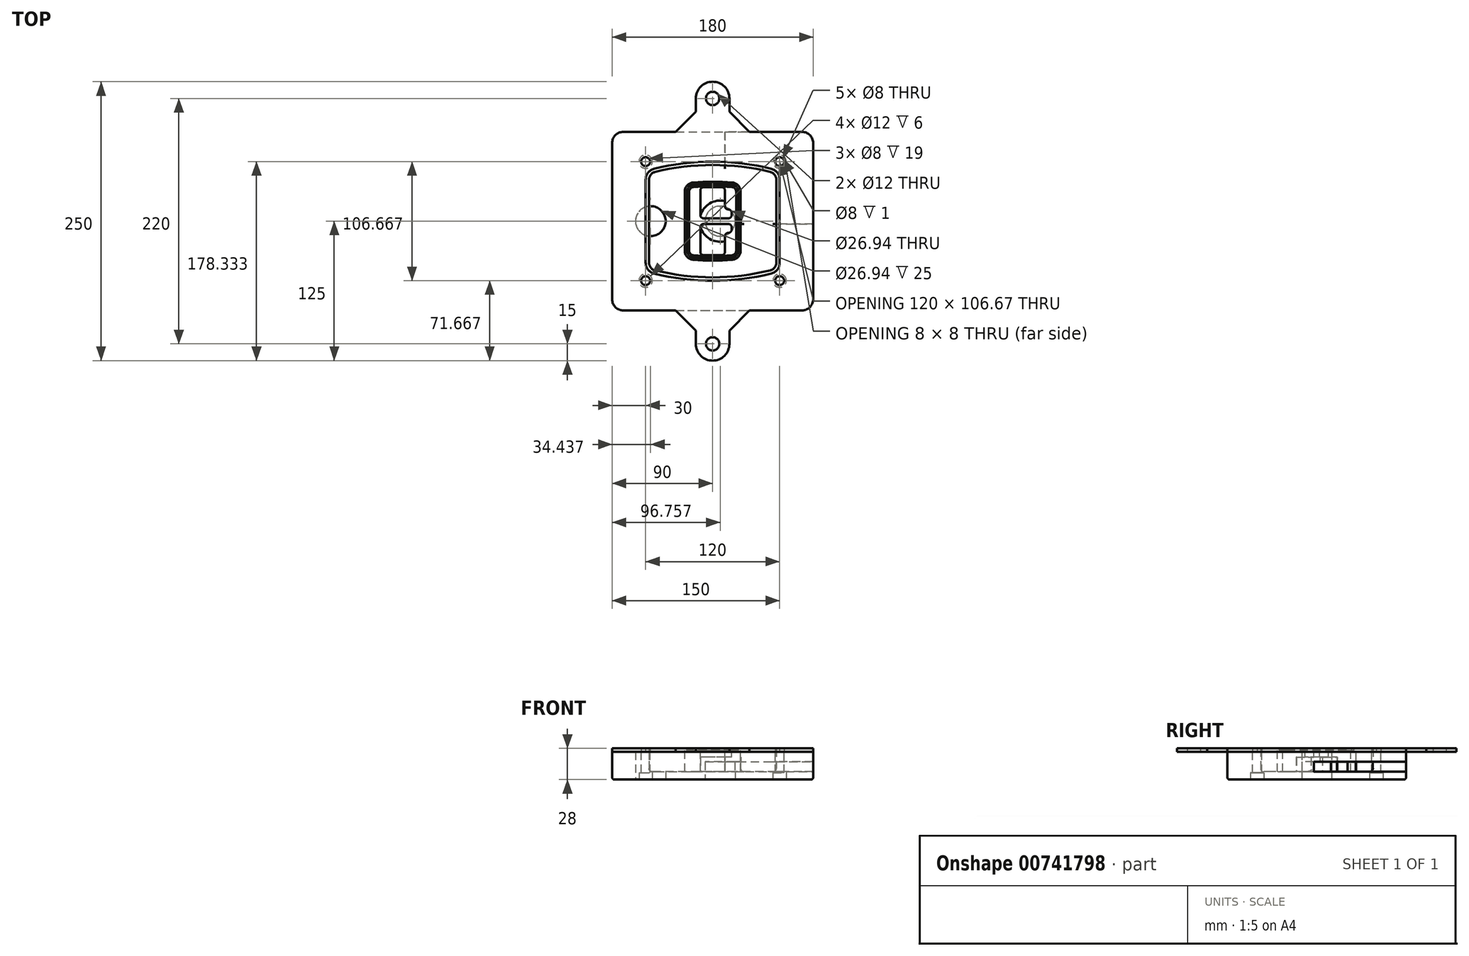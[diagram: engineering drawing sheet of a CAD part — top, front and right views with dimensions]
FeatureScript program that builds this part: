
annotation { "Feature Type Name" : "Feature", "Feature Type Description" : "" }
export const myFeature = defineFeature(function(context is Context, id is Id, definition is map)
    precondition{}
    {
        {
            var Q0;
            Q0=qCreatedBy(makeId("Top.planeOp"),FACE);
            var sketch = newSketch(context, id + "F0", { "sketchPlane" : qUnion([Q0])});
            skPoint(sketch, "E0.rect.middle", {"position": v(0, 0) * mm});
            skLineSegment(sketch, "E1.bottom", {"start": v(-80, -80) * mm, "end": v(80, -80) * mm});
            skLineSegment(sketch, "E1.top", {"start": v(-80, 80) * mm, "end": v(80, 80) * mm});
            skLineSegment(sketch, "E1.left", {"start": v(-90, -70) * mm, "end": v(-90, 70) * mm});
            skLineSegment(sketch, "E1.right", {"start": v(90, -70) * mm, "end": v(90, 70) * mm});
            skLineSegment(sketch, "E2", {"start": v(-90, 80) * mm, "end": v(90, -80) * mm, "construction": true});
            skLineSegment(sketch, "E3", {"start": v(90, 80) * mm, "end": v(-90, -80) * mm, "construction": true});
            skCircle(sketch, "E4", {"center": v(-60, 53.33) * mm, "radius": 4 * mm});
            skCircle(sketch, "E5", {"center": v(60, 53.33) * mm, "radius": 4 * mm});
            skCircle(sketch, "E6", {"center": v(60, -53.33) * mm, "radius": 4 * mm});
            skCircle(sketch, "E7", {"center": v(-60, -53.33) * mm, "radius": 4 * mm});
            skLineSegment(sketch, "E8", {"start": v(-60, 53.33) * mm, "end": v(60, 53.33) * mm, "construction": true});
            skLineSegment(sketch, "E9", {"start": v(60, 53.33) * mm, "end": v(60, -53.33) * mm, "construction": true});
            skLineSegment(sketch, "E10", {"start": v(60, -53.33) * mm, "end": v(-60, -53.33) * mm, "construction": true});
            skLineSegment(sketch, "E11", {"start": v(-60, -53.33) * mm, "end": v(-60, 53.33) * mm, "construction": true});
            skLineSegment(sketch, "E12", {"start": v(-60, 37.3) * mm, "end": v(-60, -37.3) * mm});
            skLineSegment(sketch, "E13", {"start": v(60, 37.3) * mm, "end": v(60, -37.3) * mm});
            skArc(sketch, "E14", {"start": v(52.38, 47.01) * mm, "mid": v(0, 53.33) * mm, "end": v(-52.38, 47.01) * mm});
            skArc(sketch, "E15", {"start": v(-52.38, -47.01) * mm, "mid": v(0, -53.33) * mm, "end": v(52.38, -47.01) * mm});
            skLineSegment(sketch, "E16", {"start": v(-60, 0) * mm, "end": v(60, 0) * mm, "construction": true});
            skPoint(sketch, "E17.visualSharp", {"position": v(-60, -45) * mm});
            skArc(sketch, "E17.filletArc", {"start": v(-60, -37.3) * mm, "mid": v(-57.87, -43.47) * mm, "end": v(-52.38, -47.01) * mm});
            skPoint(sketch, "E18.visualSharp", {"position": v(-60, 45) * mm});
            skArc(sketch, "E18.filletArc", {"start": v(-52.38, 47.01) * mm, "mid": v(-57.87, 43.47) * mm, "end": v(-60, 37.3) * mm});
            skPoint(sketch, "E19.visualSharp", {"position": v(60, 45) * mm});
            skArc(sketch, "E19.filletArc", {"start": v(60, 37.3) * mm, "mid": v(57.87, 43.47) * mm, "end": v(52.38, 47.01) * mm});
            skPoint(sketch, "E20.visualSharp", {"position": v(60, -45) * mm});
            skArc(sketch, "E20.filletArc", {"start": v(52.38, -47.01) * mm, "mid": v(57.87, -43.47) * mm, "end": v(60, -37.3) * mm});
            skPoint(sketch, "E21.visualSharp", {"position": v(-90, 80) * mm});
            skArc(sketch, "E21.filletArc", {"start": v(-80, 80) * mm, "mid": v(-87.07, 77.07) * mm, "end": v(-90, 70) * mm});
            skPoint(sketch, "E22.visualSharp", {"position": v(90, 80) * mm});
            skArc(sketch, "E22.filletArc", {"start": v(90, 70) * mm, "mid": v(87.07, 77.07) * mm, "end": v(80, 80) * mm});
            skPoint(sketch, "E23.visualSharp", {"position": v(90, -80) * mm});
            skArc(sketch, "E23.filletArc", {"start": v(80, -80) * mm, "mid": v(87.07, -77.07) * mm, "end": v(90, -70) * mm});
            skPoint(sketch, "E24.visualSharp", {"position": v(-90, -80) * mm});
            skArc(sketch, "E24.filletArc", {"start": v(-90, -70) * mm, "mid": v(-87.07, -77.07) * mm, "end": v(-80, -80) * mm});
            skArc(sketch, "E25.0", {"start": v(57, 37.3) * mm, "mid": v(55.5, 41.62) * mm, "end": v(51.67, 44.1) * mm});
            skLineSegment(sketch, "E25.1", {"start": v(57, 37.3) * mm, "end": v(57, -37.3) * mm});
            skArc(sketch, "E25.2", {"start": v(51.67, -44.1) * mm, "mid": v(55.5, -41.62) * mm, "end": v(57, -37.3) * mm});
            skArc(sketch, "E25.3", {"start": v(-51.67, -44.1) * mm, "mid": v(0, -50.33) * mm, "end": v(51.67, -44.1) * mm});
            skArc(sketch, "E25.4", {"start": v(-57, -37.3) * mm, "mid": v(-55.5, -41.62) * mm, "end": v(-51.67, -44.1) * mm});
            skArc(sketch, "E25.5", {"start": v(51.67, 44.1) * mm, "mid": v(0, 50.33) * mm, "end": v(-51.67, 44.1) * mm});
            skLineSegment(sketch, "E25.6", {"start": v(-57, 37.3) * mm, "end": v(-57, -37.3) * mm});
            skArc(sketch, "E25.7", {"start": v(-51.67, 44.1) * mm, "mid": v(-55.5, 41.62) * mm, "end": v(-57, 37.3) * mm});
            skArc(sketch, "E26.0", {"start": v(-53.33, 50.9) * mm, "mid": v(-61.01, 45.94) * mm, "end": v(-64, 37.3) * mm});
            skArc(sketch, "E26.1", {"start": v(53.33, 50.9) * mm, "mid": v(0, 57.33) * mm, "end": v(-53.33, 50.9) * mm});
            skArc(sketch, "E26.2", {"start": v(64, 37.3) * mm, "mid": v(61.01, 45.94) * mm, "end": v(53.33, 50.9) * mm});
            skLineSegment(sketch, "E26.3", {"start": v(64, 37.3) * mm, "end": v(64, -37.3) * mm});
            skArc(sketch, "E26.4", {"start": v(53.33, -50.9) * mm, "mid": v(61.01, -45.94) * mm, "end": v(64, -37.3) * mm});
            skLineSegment(sketch, "E26.5", {"start": v(-64, 37.3) * mm, "end": v(-64, -37.3) * mm});
            skArc(sketch, "E26.6", {"start": v(-53.33, -50.9) * mm, "mid": v(0, -57.33) * mm, "end": v(53.33, -50.9) * mm});
            skArc(sketch, "E26.7", {"start": v(-64, -37.3) * mm, "mid": v(-61.01, -45.94) * mm, "end": v(-53.33, -50.9) * mm});
            skSolve(sketch);
        }
        {
            var Q0;
            Q0=makeQuery(id+"F0.imprint","IMPRINT",FACE,{"disambiguationData":[TD([[makeQuery(id+"F0.imprint","IMPRINT",EDGE,{"derivedFrom":sQuery(id+"F0.wireOp",EDGE,"E1.bottom")}),1.0]])]});
            var Q1;
            Q1=makeQuery(id+"F0.imprint","IMPRINT",FACE,{"disambiguationData":[TD([[makeQuery(id+"F0.imprint","IMPRINT",EDGE,{"derivedFrom":sQuery(id+"F0.wireOp",EDGE,"E12")}),1.0]])]});
            var Q2;
            Q2=makeQuery(id+"F0.imprint","IMPRINT",FACE,{"disambiguationData":[TD([[makeQuery(id+"F0.imprint","IMPRINT",EDGE,{"derivedFrom":sQuery(id+"F0.wireOp",EDGE,"E25.0")}),1.0]])]});
            var Q3;
            Q3=makeQuery(id+"F0.imprint","IMPRINT",FACE,{"disambiguationData":[TD([[makeQuery(id+"F0.imprint","IMPRINT",EDGE,{"derivedFrom":sQuery(id+"F0.wireOp",EDGE,"E12")}),-1.0]])]});
            extrude(context, id + "F1", {"entities" : qUnion([Q0, Q1, Q2, Q3]), "oppositeDirection" : true, "depth" : 25 * mm, "offsetDistance" : 25 * mm});
        }
        {
            var Q0;
            Q0=makeQuery(id+"F0.imprint","IMPRINT",FACE,{"disambiguationData":[TD([[makeQuery(id+"F0.imprint","IMPRINT",EDGE,{"derivedFrom":sQuery(id+"F0.wireOp",EDGE,"E12")}),1.0]])]});
            extrude(context, id + "F2", {"entities" : qUnion([Q0]), "operationType" : NewBodyOperationType.ADD, "depth" : 3 * mm});
        }
        {
            var Q0;
            Q0=makeQuery(id+"F0.imprint","IMPRINT",FACE,{"disambiguationData":[TD([[makeQuery(id+"F0.imprint","IMPRINT",EDGE,{"derivedFrom":sQuery(id+"F0.wireOp",EDGE,"E25.0")}),1.0]])]});
            extrude(context, id + "F3", {"entities" : qUnion([Q0]), "operationType" : NewBodyOperationType.REMOVE, "oppositeDirection" : true, "depth" : 18 * mm});
        }
        {
            var Q0;
            Q0=makeQuery(id+"F2.opExtrude","CAP_FACE",FACE,{"disambiguationData":[OSD([sQuery(id+"F0.wireOp",EDGE,"E12"),sQuery(id+"F0.wireOp",EDGE,"E13"),sQuery(id+"F0.wireOp",EDGE,"E14"),sQuery(id+"F0.wireOp",EDGE,"E15"),sQuery(id+"F0.wireOp",EDGE,"E17.filletArc"),sQuery(id+"F0.wireOp",EDGE,"E18.filletArc"),sQuery(id+"F0.wireOp",EDGE,"E19.filletArc"),sQuery(id+"F0.wireOp",EDGE,"E20.filletArc"),sQuery(id+"F0.wireOp",EDGE,"E25.0"),sQuery(id+"F0.wireOp",EDGE,"E25.1"),sQuery(id+"F0.wireOp",EDGE,"E25.2"),sQuery(id+"F0.wireOp",EDGE,"E25.3"),sQuery(id+"F0.wireOp",EDGE,"E25.4"),sQuery(id+"F0.wireOp",EDGE,"E25.5"),sQuery(id+"F0.wireOp",EDGE,"E25.6"),sQuery(id+"F0.wireOp",EDGE,"E25.7")])],"isStart":false});
            var sketch = newSketch(context, id + "F4", { "sketchPlane" : qUnion([Q0])});
            skArc(sketch, "E27.0", {"start": v(-17.7, -34.56) * mm, "mid": v(0, -35.33) * mm, "end": v(17.7, -34.56) * mm});
            skArc(sketch, "E28.0", {"start": v(17.7, 34.56) * mm, "mid": v(0, 35.33) * mm, "end": v(-17.7, 34.56) * mm});
            skLineSegment(sketch, "E29", {"start": v(-25, 26.59) * mm, "end": v(-25, -26.59) * mm});
            skLineSegment(sketch, "E30", {"start": v(25, 26.59) * mm, "end": v(25, -26.59) * mm});
            skLineSegment(sketch, "E31", {"start": v(-25, 33.78) * mm, "end": v(25, 33.78) * mm, "construction": true});
            skLineSegment(sketch, "E32", {"start": v(-25, -33.78) * mm, "end": v(25, -33.78) * mm, "construction": true});
            skPoint(sketch, "E33.visualSharp", {"position": v(-25, 33.78) * mm});
            skArc(sketch, "E33.filletArc", {"start": v(-17.7, 34.56) * mm, "mid": v(-22.9, 32) * mm, "end": v(-25, 26.59) * mm});
            skPoint(sketch, "E34.visualSharp", {"position": v(25, 33.78) * mm});
            skArc(sketch, "E34.filletArc", {"start": v(25, 26.59) * mm, "mid": v(22.9, 32) * mm, "end": v(17.7, 34.56) * mm});
            skPoint(sketch, "E35.visualSharp", {"position": v(25, -33.78) * mm});
            skArc(sketch, "E35.filletArc", {"start": v(17.7, -34.56) * mm, "mid": v(22.9, -32) * mm, "end": v(25, -26.59) * mm});
            skPoint(sketch, "E36.visualSharp", {"position": v(-25, -33.78) * mm});
            skArc(sketch, "E36.filletArc", {"start": v(-25, -26.59) * mm, "mid": v(-22.9, -32) * mm, "end": v(-17.7, -34.56) * mm});
            skArc(sketch, "E37.0", {"start": v(51.67, 44.1) * mm, "mid": v(0, 50.33) * mm, "end": v(-51.67, 44.1) * mm});
            skArc(sketch, "E37.1", {"start": v(-51.67, 44.1) * mm, "mid": v(-55.5, 41.62) * mm, "end": v(-57, 37.3) * mm});
            skLineSegment(sketch, "E37.2", {"start": v(-57, 37.3) * mm, "end": v(-57, -37.3) * mm});
            skArc(sketch, "E37.3", {"start": v(-57, -37.3) * mm, "mid": v(-55.5, -41.62) * mm, "end": v(-51.67, -44.1) * mm});
            skArc(sketch, "E37.4", {"start": v(-51.67, -44.1) * mm, "mid": v(0, -50.33) * mm, "end": v(51.67, -44.1) * mm});
            skArc(sketch, "E37.5", {"start": v(51.67, -44.1) * mm, "mid": v(55.5, -41.62) * mm, "end": v(57, -37.3) * mm});
            skLineSegment(sketch, "E37.6", {"start": v(57, 37.3) * mm, "end": v(57, -37.3) * mm});
            skArc(sketch, "E37.7", {"start": v(57, 37.3) * mm, "mid": v(55.5, 41.62) * mm, "end": v(51.67, 44.1) * mm});
            skLineSegment(sketch, "E38.0", {"start": v(23, 26.59) * mm, "end": v(23, -26.59) * mm});
            skArc(sketch, "E38.1", {"start": v(17.53, -32.56) * mm, "mid": v(21.42, -30.64) * mm, "end": v(23, -26.59) * mm});
            skArc(sketch, "E38.2", {"start": v(-17.53, -32.56) * mm, "mid": v(0, -33.33) * mm, "end": v(17.53, -32.56) * mm});
            skArc(sketch, "E38.3", {"start": v(-23, -26.59) * mm, "mid": v(-21.42, -30.64) * mm, "end": v(-17.53, -32.56) * mm});
            skLineSegment(sketch, "E38.4", {"start": v(-23, 26.59) * mm, "end": v(-23, -26.59) * mm});
            skArc(sketch, "E38.5", {"start": v(23, 26.59) * mm, "mid": v(21.42, 30.64) * mm, "end": v(17.53, 32.56) * mm});
            skArc(sketch, "E38.6", {"start": v(-17.53, 32.56) * mm, "mid": v(-21.42, 30.64) * mm, "end": v(-23, 26.59) * mm});
            skArc(sketch, "E38.7", {"start": v(17.53, 32.56) * mm, "mid": v(0, 33.33) * mm, "end": v(-17.53, 32.56) * mm});
            skArc(sketch, "E39.0", {"start": v(21, 26.59) * mm, "mid": v(19.95, 29.29) * mm, "end": v(17.35, 30.57) * mm});
            skLineSegment(sketch, "E39.1", {"start": v(21, 26.59) * mm, "end": v(21, -26.59) * mm});
            skArc(sketch, "E39.2", {"start": v(17.35, -30.57) * mm, "mid": v(19.95, -29.29) * mm, "end": v(21, -26.59) * mm});
            skArc(sketch, "E39.3", {"start": v(-17.35, -30.57) * mm, "mid": v(0, -31.33) * mm, "end": v(17.35, -30.57) * mm});
            skArc(sketch, "E39.4", {"start": v(-21, -26.59) * mm, "mid": v(-19.95, -29.29) * mm, "end": v(-17.35, -30.57) * mm});
            skArc(sketch, "E39.5", {"start": v(17.35, 30.57) * mm, "mid": v(0, 31.33) * mm, "end": v(-17.35, 30.57) * mm});
            skLineSegment(sketch, "E39.6", {"start": v(-21, 26.59) * mm, "end": v(-21, -26.59) * mm});
            skArc(sketch, "E39.7", {"start": v(-17.35, 30.57) * mm, "mid": v(-19.95, 29.29) * mm, "end": v(-21, 26.59) * mm});
            skLineSegment(sketch, "E40", {"start": v(-25, 0) * mm, "end": v(25, 0) * mm, "construction": true});
            skLineSegment(sketch, "E41", {"start": v(-11, 5.5) * mm, "end": v(-11, 27.5) * mm});
            skLineSegment(sketch, "E42", {"start": v(-8, 30.5) * mm, "end": v(8, 30.5) * mm});
            skLineSegment(sketch, "E43", {"start": v(11, 27.5) * mm, "end": v(11, 13.5) * mm});
            skLineSegment(sketch, "E44", {"start": v(14, 10.5) * mm, "end": v(14, 10.5) * mm});
            skLineSegment(sketch, "E45", {"start": v(17, 7.5) * mm, "end": v(17, 5.5) * mm});
            skLineSegment(sketch, "E46", {"start": v(14, 2.5) * mm, "end": v(-8, 2.5) * mm});
            skPoint(sketch, "E47.visualSharp", {"position": v(-11, 30.5) * mm});
            skArc(sketch, "E47.filletArc", {"start": v(-8, 30.5) * mm, "mid": v(-10.12, 29.62) * mm, "end": v(-11, 27.5) * mm});
            skPoint(sketch, "E48.visualSharp", {"position": v(11, 30.5) * mm});
            skArc(sketch, "E48.filletArc", {"start": v(11, 27.5) * mm, "mid": v(10.12, 29.62) * mm, "end": v(8, 30.5) * mm});
            skPoint(sketch, "E49.visualSharp", {"position": v(11, 10.5) * mm});
            skArc(sketch, "E49.filletArc", {"start": v(11, 13.5) * mm, "mid": v(11.88, 11.38) * mm, "end": v(14, 10.5) * mm});
            skPoint(sketch, "E50.visualSharp", {"position": v(17, 10.5) * mm});
            skArc(sketch, "E50.filletArc", {"start": v(17, 7.5) * mm, "mid": v(16.12, 9.62) * mm, "end": v(14, 10.5) * mm});
            skPoint(sketch, "E51.visualSharp", {"position": v(17, 2.5) * mm});
            skArc(sketch, "E51.filletArc", {"start": v(14, 2.5) * mm, "mid": v(16.12, 3.38) * mm, "end": v(17, 5.5) * mm});
            skPoint(sketch, "E52.visualSharp", {"position": v(-11, 2.5) * mm});
            skArc(sketch, "E52.filletArc", {"start": v(-11, 5.5) * mm, "mid": v(-10.12, 3.38) * mm, "end": v(-8, 2.5) * mm});
            skLineSegment(sketch, "E53.0.MirrorCS", {"start": v(14, -2.5) * mm, "end": v(-8, -2.5) * mm});
            skArc(sketch, "E54.0.MirrorCS", {"start": v(-11, -5.5) * mm, "mid": v(-10.12, -3.38) * mm, "end": v(-8, -2.5) * mm});
            skLineSegment(sketch, "E55.0.MirrorCS", {"start": v(-11, -5.5) * mm, "end": v(-11, -27.5) * mm});
            skArc(sketch, "E56.0.MirrorCS", {"start": v(-8, -30.5) * mm, "mid": v(-10.12, -29.62) * mm, "end": v(-11, -27.5) * mm});
            skLineSegment(sketch, "E57.0.MirrorCS", {"start": v(-8, -30.5) * mm, "end": v(8, -30.5) * mm});
            skArc(sketch, "E58.0.MirrorCS", {"start": v(11, -27.5) * mm, "mid": v(10.12, -29.62) * mm, "end": v(8, -30.5) * mm});
            skLineSegment(sketch, "E59.0.MirrorCS", {"start": v(11, -27.5) * mm, "end": v(11, -13.5) * mm});
            skArc(sketch, "E60.0.MirrorCS", {"start": v(11, -13.5) * mm, "mid": v(11.88, -11.38) * mm, "end": v(14, -10.5) * mm});
            skArc(sketch, "E61.0.MirrorCS", {"start": v(17, -7.5) * mm, "mid": v(16.12, -9.62) * mm, "end": v(14, -10.5) * mm});
            skLineSegment(sketch, "E62.0.MirrorCS", {"start": v(17, -7.5) * mm, "end": v(17, -5.5) * mm});
            skArc(sketch, "E63.0.MirrorCS", {"start": v(14, -2.5) * mm, "mid": v(16.12, -3.38) * mm, "end": v(17, -5.5) * mm});
            skSolve(sketch);
        }
        {
            var Q0;
            Q0=makeQuery(id+"F4.imprint","IMPRINT",FACE,{"disambiguationData":[TD([[makeQuery(id+"F4.imprint","IMPRINT",EDGE,{"derivedFrom":sQuery(id+"F4.wireOp",EDGE,"E27.0")}),1.0]])]});
            var Q1;
            Q1=makeQuery(id+"F4.imprint","IMPRINT",FACE,{"disambiguationData":[TD([[makeQuery(id+"F4.imprint","IMPRINT",EDGE,{"derivedFrom":sQuery(id+"F4.wireOp",EDGE,"E38.0")}),-1.0]])]});
            var Q2;
            Q2=makeQuery(id+"F4.imprint","IMPRINT",FACE,{"disambiguationData":[TD([[makeQuery(id+"F4.imprint","IMPRINT",EDGE,{"derivedFrom":sQuery(id+"F4.wireOp",EDGE,"E39.0")}),1.0]])]});
            extrude(context, id + "F5", {"entities" : qUnion([Q0, Q1, Q2]), "operationType" : NewBodyOperationType.ADD, "endBound" : BoundingType.UP_TO_NEXT, "oppositeDirection" : true, "depth" : 25 * mm});
        }
        {
            var Q0;
            Q0=makeQuery(id+"F4.imprint","IMPRINT",FACE,{"disambiguationData":[TD([[makeQuery(id+"F4.imprint","IMPRINT",EDGE,{"derivedFrom":sQuery(id+"F4.wireOp",EDGE,"E38.0")}),-1.0]])]});
            extrude(context, id + "F6", {"entities" : qUnion([Q0]), "operationType" : NewBodyOperationType.REMOVE, "oppositeDirection" : true, "depth" : 2 * mm});
        }
        {
            var Q0;
            Q0=makeQuery(id+"F1.opExtrude","CAP_FACE",FACE,{"disambiguationData":[OSD([sQuery(id+"F0.wireOp",EDGE,"E1.bottom"),sQuery(id+"F0.wireOp",EDGE,"E1.top"),sQuery(id+"F0.wireOp",EDGE,"E1.left"),sQuery(id+"F0.wireOp",EDGE,"E1.right"),sQuery(id+"F0.wireOp",EDGE,"E4"),sQuery(id+"F0.wireOp",EDGE,"E5"),sQuery(id+"F0.wireOp",EDGE,"E6"),sQuery(id+"F0.wireOp",EDGE,"E7"),sQuery(id+"F0.wireOp",EDGE,"E21.filletArc"),sQuery(id+"F0.wireOp",EDGE,"E22.filletArc"),sQuery(id+"F0.wireOp",EDGE,"E23.filletArc"),sQuery(id+"F0.wireOp",EDGE,"E24.filletArc")])],"isStart":false});
            var sketch = newSketch(context, id + "F7", { "sketchPlane" : qUnion([Q0])});
            skCircle(sketch, "E64", {"center": v(6.76, 0) * mm, "radius": 13.47 * mm});
            skCircle(sketch, "E65", {"center": v(-55.56, 0) * mm, "radius": 13.47 * mm});
            skLineSegment(sketch, "E66", {"start": v(90, 0) * mm, "end": v(-90, 0) * mm});
            skCircle(sketch, "E67", {"center": v(6.76, 0) * mm, "radius": 18.47 * mm});
            skCircle(sketch, "E68", {"center": v(60, -53.33) * mm, "radius": 6 * mm});
            skCircle(sketch, "E69", {"center": v(-60, -53.33) * mm, "radius": 6 * mm});
            skCircle(sketch, "E70", {"center": v(-60, 53.33) * mm, "radius": 6 * mm});
            skCircle(sketch, "E71", {"center": v(60, 53.33) * mm, "radius": 6 * mm});
            skSolve(sketch);
        }
        {
            var Q0;
            {var subQ1=sQuery(id+"F7.wireOp",EDGE,"E66");var subQ4=sQuery(id+"F7.wireOp",EDGE,"E64");var subQ6=makeQuery(id+"F7.imprint","INTERSECT",VERTEX,{"disambiguationData":[OD(0.0)],"derivedFrom":[subQ4,subQ1]});Q0=makeQuery(id+"F7.imprint","IMPRINT",FACE,{"disambiguationData":[TD([[makeQuery(id+"F7.imprint","IMPRINT",EDGE,{"disambiguationData":[TD([[subQ6,-1.0]])],"derivedFrom":subQ4}),-1.0]])]});}
            var Q1;
            {var subQ0=sQuery(id+"F7.wireOp",EDGE,"E66");var subQ1=sQuery(id+"F7.wireOp",EDGE,"E64");var subQ3=makeQuery(id+"F7.imprint","INTERSECT",VERTEX,{"disambiguationData":[OD(0.0)],"derivedFrom":[subQ1,subQ0]});Q1=makeQuery(id+"F7.imprint","IMPRINT",FACE,{"disambiguationData":[TD([[makeQuery(id+"F7.imprint","IMPRINT",EDGE,{"disambiguationData":[TD([[subQ3,-1.0]])],"derivedFrom":subQ1}),1.0]])]});}
            var Q2;
            {var subQ0=sQuery(id+"F7.wireOp",EDGE,"E66");var subQ1=sQuery(id+"F7.wireOp",EDGE,"E64");var subQ3=makeQuery(id+"F7.imprint","INTERSECT",VERTEX,{"disambiguationData":[OD(0.0)],"derivedFrom":[subQ1,subQ0]});Q2=makeQuery(id+"F7.imprint","IMPRINT",FACE,{"disambiguationData":[TD([[makeQuery(id+"F7.imprint","IMPRINT",EDGE,{"disambiguationData":[TD([[subQ3,1.0]])],"derivedFrom":subQ1}),1.0]])]});}
            var Q3;
            {var subQ1=sQuery(id+"F7.wireOp",EDGE,"E66");var subQ4=sQuery(id+"F7.wireOp",EDGE,"E64");var subQ6=makeQuery(id+"F7.imprint","INTERSECT",VERTEX,{"disambiguationData":[OD(0.0)],"derivedFrom":[subQ4,subQ1]});Q3=makeQuery(id+"F7.imprint","IMPRINT",FACE,{"disambiguationData":[TD([[makeQuery(id+"F7.imprint","IMPRINT",EDGE,{"disambiguationData":[TD([[subQ6,1.0]])],"derivedFrom":subQ4}),-1.0]])]});}
            extrude(context, id + "F8", {"entities" : qUnion([Q0, Q1, Q2, Q3]), "operationType" : NewBodyOperationType.ADD, "oppositeDirection" : true, "depth" : 20 * mm});
        }
        {
            var Q0;
            {var subQ0=sQuery(id+"F7.wireOp",EDGE,"E66");var subQ1=sQuery(id+"F7.wireOp",EDGE,"E64");var subQ3=makeQuery(id+"F7.imprint","INTERSECT",VERTEX,{"disambiguationData":[OD(0.0)],"derivedFrom":[subQ1,subQ0]});Q0=makeQuery(id+"F7.imprint","IMPRINT",FACE,{"disambiguationData":[TD([[makeQuery(id+"F7.imprint","IMPRINT",EDGE,{"disambiguationData":[TD([[subQ3,-1.0]])],"derivedFrom":subQ1}),1.0]])]});}
            var Q1;
            {var subQ0=sQuery(id+"F7.wireOp",EDGE,"E66");var subQ1=sQuery(id+"F7.wireOp",EDGE,"E64");var subQ3=makeQuery(id+"F7.imprint","INTERSECT",VERTEX,{"disambiguationData":[OD(0.0)],"derivedFrom":[subQ1,subQ0]});Q1=makeQuery(id+"F7.imprint","IMPRINT",FACE,{"disambiguationData":[TD([[makeQuery(id+"F7.imprint","IMPRINT",EDGE,{"disambiguationData":[TD([[subQ3,1.0]])],"derivedFrom":subQ1}),1.0]])]});}
            extrude(context, id + "F9", {"entities" : qUnion([Q0, Q1]), "operationType" : NewBodyOperationType.REMOVE, "oppositeDirection" : true, "depth" : 16 * mm});
        }
        {
            var Q0;
            {var subQ0=sQuery(id+"F7.wireOp",EDGE,"E66");var subQ1=sQuery(id+"F7.wireOp",EDGE,"E65");var subQ3=makeQuery(id+"F7.imprint","INTERSECT",VERTEX,{"disambiguationData":[OD(0.0)],"derivedFrom":[subQ1,subQ0]});Q0=makeQuery(id+"F7.imprint","IMPRINT",FACE,{"disambiguationData":[TD([[makeQuery(id+"F7.imprint","IMPRINT",EDGE,{"disambiguationData":[TD([[subQ3,-1.0]])],"derivedFrom":subQ1}),1.0]])]});}
            var Q1;
            {var subQ0=sQuery(id+"F7.wireOp",EDGE,"E66");var subQ1=sQuery(id+"F7.wireOp",EDGE,"E65");var subQ3=makeQuery(id+"F7.imprint","INTERSECT",VERTEX,{"disambiguationData":[OD(0.0)],"derivedFrom":[subQ1,subQ0]});Q1=makeQuery(id+"F7.imprint","IMPRINT",FACE,{"disambiguationData":[TD([[makeQuery(id+"F7.imprint","IMPRINT",EDGE,{"disambiguationData":[TD([[subQ3,1.0]])],"derivedFrom":subQ1}),1.0]])]});}
            extrude(context, id + "F10", {"entities" : qUnion([Q0, Q1]), "operationType" : NewBodyOperationType.REMOVE, "oppositeDirection" : true, "depth" : 25 * mm});
        }
        {
            var Q0;
            Q0=makeQuery(id+"F7.imprint","IMPRINT",FACE,{"disambiguationData":[TD([[makeQuery(id+"F7.imprint","IMPRINT",EDGE,{"derivedFrom":sQuery(id+"F7.wireOp",EDGE,"E68")}),1.0]])]});
            var Q1;
            Q1=makeQuery(id+"F7.imprint","IMPRINT",FACE,{"disambiguationData":[TD([[makeQuery(id+"F7.imprint","IMPRINT",EDGE,{"derivedFrom":makeQuery(id+"F1.opExtrude","CAP_EDGE",EDGE,{"disambiguationData":[OSD([sQuery(id+"F0.wireOp",EDGE,"E5")])],"isStart":false})}),-1.0]])]});
            var Q2;
            Q2=makeQuery(id+"F7.imprint","IMPRINT",FACE,{"disambiguationData":[TD([[makeQuery(id+"F7.imprint","IMPRINT",EDGE,{"derivedFrom":sQuery(id+"F7.wireOp",EDGE,"E69")}),1.0]])]});
            var Q3;
            Q3=makeQuery(id+"F7.imprint","IMPRINT",FACE,{"disambiguationData":[TD([[makeQuery(id+"F7.imprint","IMPRINT",EDGE,{"derivedFrom":makeQuery(id+"F1.opExtrude","CAP_EDGE",EDGE,{"disambiguationData":[OSD([sQuery(id+"F0.wireOp",EDGE,"E4")])],"isStart":false})}),-1.0]])]});
            var Q4;
            Q4=makeQuery(id+"F7.imprint","IMPRINT",FACE,{"disambiguationData":[TD([[makeQuery(id+"F7.imprint","IMPRINT",EDGE,{"derivedFrom":sQuery(id+"F7.wireOp",EDGE,"E70")}),1.0]])]});
            var Q5;
            Q5=makeQuery(id+"F7.imprint","IMPRINT",FACE,{"disambiguationData":[TD([[makeQuery(id+"F7.imprint","IMPRINT",EDGE,{"derivedFrom":makeQuery(id+"F1.opExtrude","CAP_EDGE",EDGE,{"disambiguationData":[OSD([sQuery(id+"F0.wireOp",EDGE,"E7")])],"isStart":false})}),-1.0]])]});
            var Q6;
            Q6=makeQuery(id+"F7.imprint","IMPRINT",FACE,{"disambiguationData":[TD([[makeQuery(id+"F7.imprint","IMPRINT",EDGE,{"derivedFrom":sQuery(id+"F7.wireOp",EDGE,"E71")}),1.0]])]});
            var Q7;
            Q7=makeQuery(id+"F7.imprint","IMPRINT",FACE,{"disambiguationData":[TD([[makeQuery(id+"F7.imprint","IMPRINT",EDGE,{"derivedFrom":makeQuery(id+"F1.opExtrude","CAP_EDGE",EDGE,{"disambiguationData":[OSD([sQuery(id+"F0.wireOp",EDGE,"E6")])],"isStart":false})}),-1.0]])]});
            extrude(context, id + "F11", {"entities" : qUnion([Q0, Q1, Q2, Q3, Q4, Q5, Q6, Q7]), "operationType" : NewBodyOperationType.REMOVE, "oppositeDirection" : true, "depth" : 6 * mm});
        }
        {
            var Q0;
            Q0=makeQuery(id+"F9.boolean.opBoolean","COPY",FACE,{"derivedFrom":makeQuery(id+"F9.opExtrude","CAP_FACE",FACE,{"disambiguationData":[OSD([sQuery(id+"F7.wireOp",EDGE,"E64")])],"isStart":false})});
            var sketch = newSketch(context, id + "F12", { "sketchPlane" : qUnion([Q0])});
            skArc(sketch, "E72.0", {"start": v(11, -88.19) * mm, "mid": v(97.1, -83.6) * mm, "end": v(92.5, 2.5) * mm});
            skLineSegment(sketch, "E72.1", {"start": v(11, -17.97) * mm, "end": v(11, -17.97) * mm});
            skLineSegment(sketch, "E73", {"start": v(92.5, -105.13) * mm, "end": v(102.3, -105.13) * mm});
            skLineSegment(sketch, "E74.0", {"start": v(92.5, 2.5) * mm, "end": v(14, 2.5) * mm});
            skArc(sketch, "E74.1", {"start": v(14, 2.5) * mm, "mid": v(16.12, 3.38) * mm, "end": v(17, 5.5) * mm});
            skLineSegment(sketch, "E74.2", {"start": v(17, 7.5) * mm, "end": v(17, 5.5) * mm});
            skArc(sketch, "E74.3", {"start": v(17, 7.5) * mm, "mid": v(16.12, 9.62) * mm, "end": v(14, 10.5) * mm});
            skArc(sketch, "E74.4", {"start": v(11, 13.5) * mm, "mid": v(11.88, 11.38) * mm, "end": v(14, 10.5) * mm});
            skLineSegment(sketch, "E74.5", {"start": v(11, 13.5) * mm, "end": v(11, -88.19) * mm});
            skLineSegment(sketch, "E74.7", {"start": v(92.5, -2.5) * mm, "end": v(14, -2.5) * mm});
            skArc(sketch, "E74.8", {"start": v(14, -2.5) * mm, "mid": v(16.12, -3.38) * mm, "end": v(17, -5.5) * mm});
            skLineSegment(sketch, "E74.9", {"start": v(17, -7.5) * mm, "end": v(17, -5.5) * mm});
            skArc(sketch, "E74.10", {"start": v(17, -7.5) * mm, "mid": v(16.12, -9.62) * mm, "end": v(14, -10.5) * mm});
            skArc(sketch, "E74.11", {"start": v(11, -13.5) * mm, "mid": v(11.88, -11.38) * mm, "end": v(14, -10.5) * mm});
            skLineSegment(sketch, "E74.12", {"start": v(11, -17.97) * mm, "end": v(11, -13.5) * mm});
            skPoint(sketch, "E75.orphan", {"position": v(11, -27.5) * mm});
            skPoint(sketch, "E76.orphan", {"position": v(-8, -2.5) * mm});
            skPoint(sketch, "E77.orphan", {"position": v(-8, 2.5) * mm});
            skPoint(sketch, "E78.orphan", {"position": v(11, 27.5) * mm});
            skSolve(sketch);
        }
        {
            var Q0;
            {var subQ7=sQuery(id+"F12.wireOp",EDGE,"E72.0");var subQ14=sQuery(id+"F12.wireOp",EDGE,"E72.1");var subQ16=sQuery(id+"F12.wireOp",EDGE,"E74.1");var subQ18=sQuery(id+"F12.wireOp",EDGE,"E74.8");Q0=qUnion([makeQuery(id+"F12.imprint","IMPRINT",FACE,{"disambiguationData":[TD([[makeQuery(id+"F12.imprint","IMPRINT",EDGE,{"derivedFrom":subQ7}),1.0]])]}),makeQuery(id+"F12.imprint","IMPRINT",FACE,{"disambiguationData":[TD([[makeQuery(id+"F12.imprint","IMPRINT",EDGE,{"derivedFrom":subQ14}),1.0]])]}),makeQuery(id+"F12.imprint","IMPRINT",FACE,{"disambiguationData":[TD([[makeQuery(id+"F12.imprint","IMPRINT",EDGE,{"derivedFrom":subQ16}),1.0]])]}),makeQuery(id+"F12.imprint","IMPRINT",FACE,{"disambiguationData":[TD([[makeQuery(id+"F12.imprint","IMPRINT",EDGE,{"derivedFrom":subQ18}),-1.0]])]})]);}
            var Q1;
            Q1=makeQuery(id+"F5.boolean.opBoolean","SPLIT",FACE,{"disambiguationData":[TD([makeQuery(id+"F5.opExtrude","SWEPT_FACE",FACE,{"disambiguationData":[OSD([sQuery(id+"F4.wireOp",EDGE,"E41")])]})])],"derivedFrom":makeQuery(id+"F3.boolean.opBoolean","COPY",FACE,{"derivedFrom":makeQuery(id+"F3.opExtrude","CAP_FACE",FACE,{"disambiguationData":[OSD([sQuery(id+"F0.wireOp",EDGE,"E25.0"),sQuery(id+"F0.wireOp",EDGE,"E25.1"),sQuery(id+"F0.wireOp",EDGE,"E25.2"),sQuery(id+"F0.wireOp",EDGE,"E25.3"),sQuery(id+"F0.wireOp",EDGE,"E25.4"),sQuery(id+"F0.wireOp",EDGE,"E25.5"),sQuery(id+"F0.wireOp",EDGE,"E25.6"),sQuery(id+"F0.wireOp",EDGE,"E25.7")])],"isStart":false})})});
            extrude(context, id + "F13", {"entities" : qUnion([Q0]), "operationType" : NewBodyOperationType.REMOVE, "endBound" : BoundingType.UP_TO_SURFACE, "endBoundEntityFace" : qUnion([Q1]), "depth" : 25 * mm});
        }
        {
            var Q0;
            Q0=makeQuery(id+"F3.boolean.opBoolean","COPY",EDGE,{"derivedFrom":makeQuery(id+"F3.opExtrude","CAP_EDGE",EDGE,{"disambiguationData":[OSD([sQuery(id+"F0.wireOp",EDGE,"E25.6")])],"isStart":false})});
            var Q1;
            Q1=makeQuery(id+"F8.boolean.opBoolean","INTERSECT",EDGE,{"derivedFrom":[makeQuery(id+"F5.opExtrude","SWEPT_FACE",FACE,{"disambiguationData":[OSD([sQuery(id+"F4.wireOp",EDGE,"E30")])]}),makeQuery(id+"F8.opExtrude","CAP_FACE",FACE,{"disambiguationData":[OSD([sQuery(id+"F7.wireOp",EDGE,"E67")])],"isStart":false})]});
            var Q2;
            Q2=makeQuery(id+"F8.boolean.opBoolean","INTERSECT",EDGE,{"disambiguationData":[OD(1.0)],"derivedFrom":[makeQuery(id+"F5.opExtrude","SWEPT_FACE",FACE,{"disambiguationData":[OSD([sQuery(id+"F4.wireOp",EDGE,"E30")])]}),makeQuery(id+"F8.opExtrude","SWEPT_FACE",FACE,{"disambiguationData":[OSD([sQuery(id+"F7.wireOp",EDGE,"E67")])]})]});
            var Q3;
            {var subQ0=makeQuery(id+"F3.boolean.opBoolean","COPY",FACE,{"derivedFrom":makeQuery(id+"F3.opExtrude","CAP_FACE",FACE,{"disambiguationData":[OSD([sQuery(id+"F0.wireOp",EDGE,"E25.0"),sQuery(id+"F0.wireOp",EDGE,"E25.1"),sQuery(id+"F0.wireOp",EDGE,"E25.2"),sQuery(id+"F0.wireOp",EDGE,"E25.3"),sQuery(id+"F0.wireOp",EDGE,"E25.4"),sQuery(id+"F0.wireOp",EDGE,"E25.5"),sQuery(id+"F0.wireOp",EDGE,"E25.6"),sQuery(id+"F0.wireOp",EDGE,"E25.7")])],"isStart":false})});var subQ1=sQuery(id+"F4.wireOp",EDGE,"E30");Q3=makeQuery(id+"F8.boolean.opBoolean","SPLIT",EDGE,{"disambiguationData":[TD([makeQuery(id+"F5.opExtrude","SWEPT_FACE",FACE,{"disambiguationData":[OSD([sQuery(id+"F4.wireOp",EDGE,"E35.filletArc")])]})])],"derivedFrom":makeQuery(id+"F5.opExtrude","TWEAK_EDGE",EDGE,{"derivedFrom":[subQ0,makeQuery(id+"F4.imprint","IMPRINT",EDGE,{"derivedFrom":subQ1})]})});}
            var Q4;
            {var subQ0=sQuery(id+"F0.wireOp",EDGE,"E25.0");var subQ1=sQuery(id+"F0.wireOp",EDGE,"E25.1");var subQ2=sQuery(id+"F0.wireOp",EDGE,"E25.2");var subQ3=sQuery(id+"F0.wireOp",EDGE,"E25.3");var subQ4=sQuery(id+"F0.wireOp",EDGE,"E25.4");var subQ5=sQuery(id+"F0.wireOp",EDGE,"E25.5");var subQ6=sQuery(id+"F0.wireOp",EDGE,"E25.6");var subQ7=sQuery(id+"F0.wireOp",EDGE,"E25.7");Q4=makeQuery(id+"F8.boolean.opBoolean","INTERSECT",EDGE,{"derivedFrom":[makeQuery(id+"F5.boolean.opBoolean","SPLIT",FACE,{"disambiguationData":[TD([makeQuery(id+"F2.opExtrude","SWEPT_FACE",FACE,{"disambiguationData":[OSD([subQ0])]})])],"derivedFrom":makeQuery(id+"F3.boolean.opBoolean","COPY",FACE,{"derivedFrom":makeQuery(id+"F3.opExtrude","CAP_FACE",FACE,{"disambiguationData":[OSD([subQ0,subQ1,subQ2,subQ3,subQ4,subQ5,subQ6,subQ7])],"isStart":false})})}),makeQuery(id+"F8.opExtrude","SWEPT_FACE",FACE,{"disambiguationData":[OSD([sQuery(id+"F7.wireOp",EDGE,"E67")])]})]});}
            var Q5;
            Q5=makeQuery(id+"F8.boolean.opBoolean","INTERSECT",EDGE,{"disambiguationData":[OD(0.0)],"derivedFrom":[makeQuery(id+"F5.opExtrude","SWEPT_FACE",FACE,{"disambiguationData":[OSD([sQuery(id+"F4.wireOp",EDGE,"E30")])]}),makeQuery(id+"F8.opExtrude","SWEPT_FACE",FACE,{"disambiguationData":[OSD([sQuery(id+"F7.wireOp",EDGE,"E67")])]})]});
            fillet(context, id + "F14", {"entities" : qUnion([Q0, Q1, Q2, Q3, Q4, Q5]), "radius" : 3 * mm, "tangentPropagation" : true, "allowEdgeOverflow" : false});
        }
        {
            var Q0;
            Q0=makeQuery(id+"F1.opExtrude","CAP_EDGE",EDGE,{"disambiguationData":[OSD([sQuery(id+"F0.wireOp",EDGE,"E1.bottom")])],"isStart":false});
            fillet(context, id + "F15", {"entities" : qUnion([Q0]), "radius" : 2 * mm, "tangentPropagation" : true, "allowEdgeOverflow" : false});
        }
        {
            var Q0;
            {var subQ0=sQuery(id+"F0.wireOp",EDGE,"E21.filletArc");var subQ1=sQuery(id+"F0.wireOp",EDGE,"E7");var subQ2=sQuery(id+"F0.wireOp",EDGE,"E6");var subQ3=sQuery(id+"F0.wireOp",EDGE,"E5");var subQ4=sQuery(id+"F0.wireOp",EDGE,"E4");var subQ5=sQuery(id+"F0.wireOp",EDGE,"E22.filletArc");var subQ6=sQuery(id+"F0.wireOp",EDGE,"E1.bottom");var subQ7=sQuery(id+"F0.wireOp",EDGE,"E1.right");var subQ8=sQuery(id+"F0.wireOp",EDGE,"E1.top");var subQ9=sQuery(id+"F0.wireOp",EDGE,"E1.left");var subQ10=sQuery(id+"F0.wireOp",EDGE,"E23.filletArc");var subQ11=sQuery(id+"F0.wireOp",EDGE,"E24.filletArc");Q0=makeQuery(id+"F2.boolean.opBoolean","SPLIT",FACE,{"disambiguationData":[TD([makeQuery(id+"F1.opExtrude","SWEPT_FACE",FACE,{"disambiguationData":[OSD([subQ6])]})])],"derivedFrom":makeQuery(id+"F1.opExtrude","CAP_FACE",FACE,{"disambiguationData":[OSD([subQ6,subQ8,subQ9,subQ7,subQ4,subQ3,subQ2,subQ1,subQ0,subQ5,subQ10,subQ11])],"isStart":true})});}
            var sketch = newSketch(context, id + "F16", { "sketchPlane" : qUnion([Q0])});
            skLineSegment(sketch, "E79.0", {"start": v(-80, 80) * mm, "end": v(80, 80) * mm});
            skArc(sketch, "E79.1", {"start": v(-80, 80) * mm, "mid": v(-87.07, 77.07) * mm, "end": v(-90, 70) * mm});
            skArc(sketch, "E79.2", {"start": v(90, 70) * mm, "mid": v(87.07, 77.07) * mm, "end": v(80, 80) * mm});
            skLineSegment(sketch, "E79.3", {"start": v(90, -70) * mm, "end": v(90, 70) * mm});
            skLineSegment(sketch, "E79.4", {"start": v(-80, -80) * mm, "end": v(80, -80) * mm});
            skArc(sketch, "E79.5", {"start": v(-90, -70) * mm, "mid": v(-87.07, -77.07) * mm, "end": v(-80, -80) * mm});
            skLineSegment(sketch, "E79.6", {"start": v(-90, -70) * mm, "end": v(-90, 70) * mm});
            skCircle(sketch, "E79.7", {"center": v(-60, 53.33) * mm, "radius": 4 * mm});
            skCircle(sketch, "E79.8", {"center": v(60, 53.33) * mm, "radius": 4 * mm});
            skCircle(sketch, "E79.9", {"center": v(60, -53.33) * mm, "radius": 4 * mm});
            skArc(sketch, "E79.10", {"start": v(80, -80) * mm, "mid": v(87.07, -77.07) * mm, "end": v(90, -70) * mm});
            skCircle(sketch, "E79.11", {"center": v(-60, -53.33) * mm, "radius": 4 * mm});
            skArc(sketch, "E79.12", {"start": v(52.38, 47.01) * mm, "mid": v(0, 53.33) * mm, "end": v(-52.38, 47.01) * mm});
            skLineSegment(sketch, "E79.13", {"start": v(60, 37.3) * mm, "end": v(60, -37.3) * mm});
            skArc(sketch, "E79.14", {"start": v(60, 37.3) * mm, "mid": v(57.87, 43.47) * mm, "end": v(52.38, 47.01) * mm});
            skLineSegment(sketch, "E79.15", {"start": v(-60, 37.3) * mm, "end": v(-60, -37.3) * mm});
            skArc(sketch, "E79.16", {"start": v(-52.38, -47.01) * mm, "mid": v(0, -53.33) * mm, "end": v(52.38, -47.01) * mm});
            skArc(sketch, "E79.17", {"start": v(-60, -37.3) * mm, "mid": v(-57.87, -43.47) * mm, "end": v(-52.38, -47.01) * mm});
            skArc(sketch, "E79.18", {"start": v(52.38, -47.01) * mm, "mid": v(57.87, -43.47) * mm, "end": v(60, -37.3) * mm});
            skArc(sketch, "E79.19", {"start": v(-52.38, 47.01) * mm, "mid": v(-57.87, 43.47) * mm, "end": v(-60, 37.3) * mm});
            skLineSegment(sketch, "E80", {"start": v(-33, 80) * mm, "end": v(-15, 98) * mm});
            skLineSegment(sketch, "E81", {"start": v(-15, 98) * mm, "end": v(-15, 110) * mm});
            skLineSegment(sketch, "E82", {"start": v(0, 110) * mm, "end": v(0, 80) * mm, "construction": true});
            skLineSegment(sketch, "E83", {"start": v(33, 80) * mm, "end": v(15, 98) * mm});
            skLineSegment(sketch, "E84", {"start": v(15, 98) * mm, "end": v(15, 110) * mm});
            skArc(sketch, "E85", {"start": v(15, 110) * mm, "mid": v(0, 125) * mm, "end": v(-15, 110) * mm});
            skCircle(sketch, "E86", {"center": v(0, 110) * mm, "radius": 6 * mm});
            skLineSegment(sketch, "E87", {"start": v(-90, 0) * mm, "end": v(90, 0) * mm, "construction": true});
            skLineSegment(sketch, "E88.MirrorCS", {"start": v(0, -110) * mm, "end": v(0, -80) * mm, "construction": true});
            skLineSegment(sketch, "E89.MirrorCS", {"start": v(33, -80) * mm, "end": v(15, -98) * mm});
            skLineSegment(sketch, "E90.MirrorCS", {"start": v(15, -98) * mm, "end": v(15, -110) * mm});
            skLineSegment(sketch, "E91.MirrorCS", {"start": v(-33, -80) * mm, "end": v(-15, -98) * mm});
            skLineSegment(sketch, "E92.MirrorCS", {"start": v(-15, -98) * mm, "end": v(-15, -110) * mm});
            skArc(sketch, "E93.MirrorCS", {"start": v(15, -110) * mm, "mid": v(0, -125) * mm, "end": v(-15, -110) * mm});
            skCircle(sketch, "E94.MirrorC", {"center": v(0, -110) * mm, "radius": 6 * mm});
            skSolve(sketch);
        }
        {
            var Q0;
            Q0 = qSketchRegion(id + "F16", true);
            var Q1;
            Q1=makeQuery(id+"F2.opExtrude","CAP_FACE",FACE,{"disambiguationData":[OSD([sQuery(id+"F0.wireOp",EDGE,"E12"),sQuery(id+"F0.wireOp",EDGE,"E13"),sQuery(id+"F0.wireOp",EDGE,"E14"),sQuery(id+"F0.wireOp",EDGE,"E15"),sQuery(id+"F0.wireOp",EDGE,"E17.filletArc"),sQuery(id+"F0.wireOp",EDGE,"E18.filletArc"),sQuery(id+"F0.wireOp",EDGE,"E19.filletArc"),sQuery(id+"F0.wireOp",EDGE,"E20.filletArc"),sQuery(id+"F0.wireOp",EDGE,"E25.0"),sQuery(id+"F0.wireOp",EDGE,"E25.1"),sQuery(id+"F0.wireOp",EDGE,"E25.2"),sQuery(id+"F0.wireOp",EDGE,"E25.3"),sQuery(id+"F0.wireOp",EDGE,"E25.4"),sQuery(id+"F0.wireOp",EDGE,"E25.5"),sQuery(id+"F0.wireOp",EDGE,"E25.6"),sQuery(id+"F0.wireOp",EDGE,"E25.7")])],"isStart":false});
            extrude(context, id + "F17", {"entities" : qUnion([Q0]), "endBound" : BoundingType.UP_TO_SURFACE, "depth" : 25 * mm, "endBoundEntityFace" : qUnion([Q1]), "offsetDistance" : 25 * mm});
        }
    });
